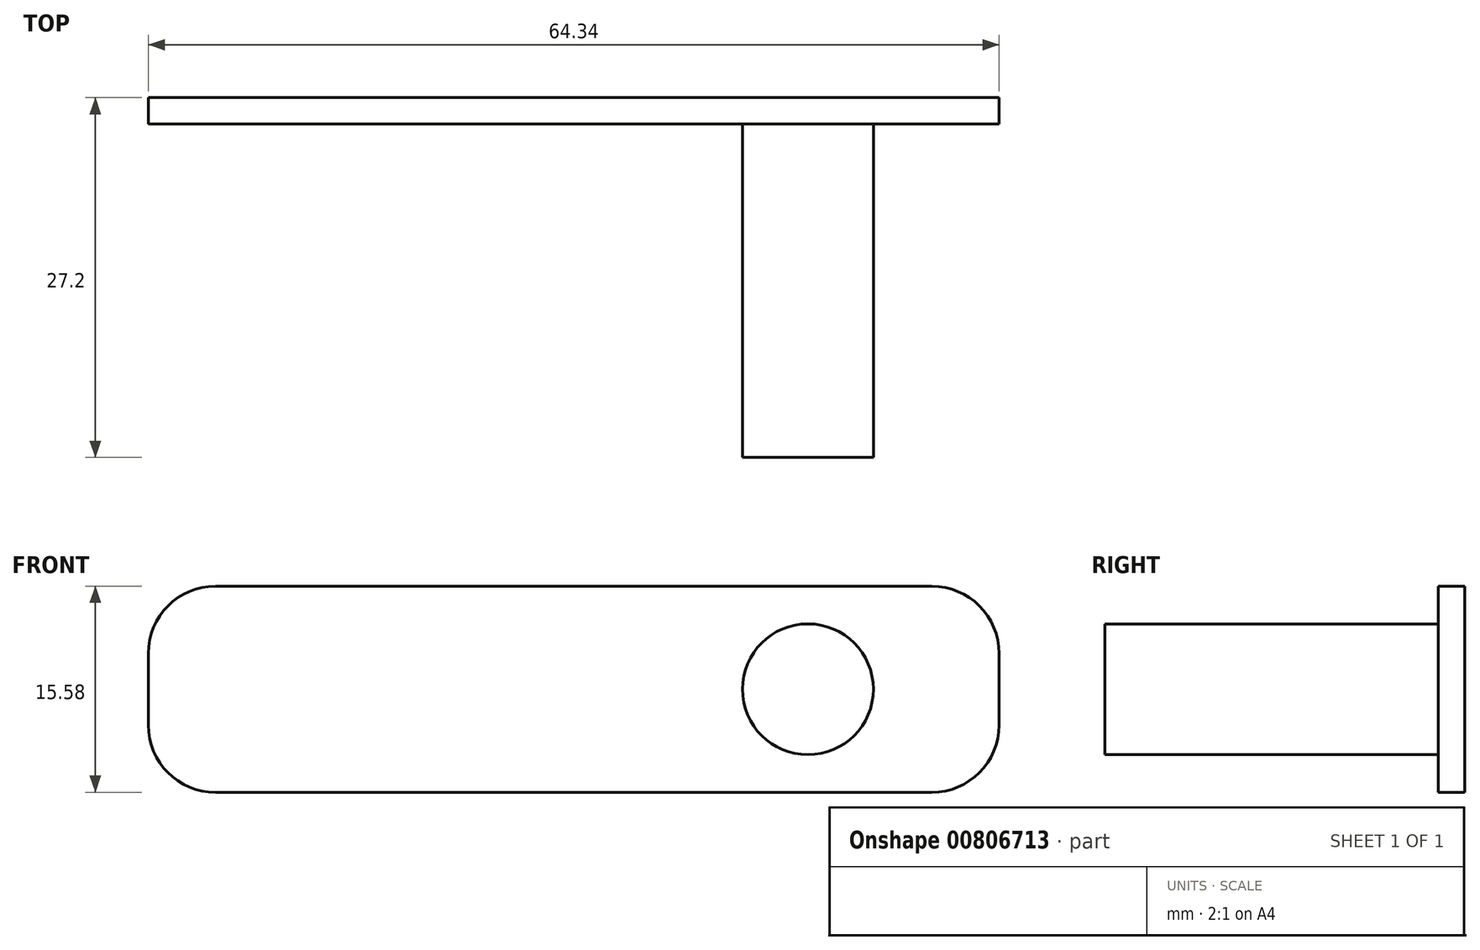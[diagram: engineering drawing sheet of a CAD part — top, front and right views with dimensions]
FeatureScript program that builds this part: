
annotation { "Feature Type Name" : "Feature", "Feature Type Description" : "" }
export const myFeature = defineFeature(function(context is Context, id is Id, definition is map)
    precondition{}
    {
        {
            var Q0;
            Q0=qCreatedBy(makeId("Front.planeOp"),FACE);
            var sketch = newSketch(context, id + "F0", { "sketchPlane" : qUnion([Q0])});
            skLineSegment(sketch, "E0.bottom", {"start": v(32.17, -7.8) * mm, "end": v(-32.17, -7.8) * mm});
            skLineSegment(sketch, "E0.top", {"start": v(32.17, 7.8) * mm, "end": v(-32.17, 7.8) * mm});
            skLineSegment(sketch, "E0.left", {"start": v(32.17, -7.8) * mm, "end": v(32.17, 7.8) * mm});
            skLineSegment(sketch, "E0.right", {"start": v(-32.17, -7.8) * mm, "end": v(-32.17, 7.8) * mm});
            skPoint(sketch, "E0.middle", {"position": v(0, 0) * mm});
            skSolve(sketch);
        }
        {
            var Q0;
            Q0=makeQuery(id+"F0.imprint","IMPRINT",FACE,{"disambiguationData":[TD([[makeQuery(id+"F0.imprint","IMPRINT",EDGE,{"derivedFrom":sQuery(id+"F0.wireOp",EDGE,"E0.bottom")}),-1.0]])]});
            extrude(context, id + "F1", {"entities" : qUnion([Q0]), "depth" : 2 * mm, "offsetDistance" : 25.4 * mm});
        }
        {
            var Q0;
            Q0=makeQuery(id+"F1.opExtrude","CAP_FACE",FACE,{"disambiguationData":[OSD([sQuery(id+"F0.wireOp",EDGE,"E0.bottom"),sQuery(id+"F0.wireOp",EDGE,"E0.top"),sQuery(id+"F0.wireOp",EDGE,"E0.left"),sQuery(id+"F0.wireOp",EDGE,"E0.right")])],"isStart":false});
            var sketch = newSketch(context, id + "F2", { "sketchPlane" : qUnion([Q0])});
            skCircle(sketch, "E1", {"center": v(17.71, 0) * mm, "radius": 4.95 * mm});
            skSolve(sketch);
        }
        {
            var Q0;
            Q0=makeQuery(id+"F2.imprint","IMPRINT",FACE,{"disambiguationData":[TD([[makeQuery(id+"F2.imprint","IMPRINT",EDGE,{"derivedFrom":sQuery(id+"F2.wireOp",EDGE,"E1")}),1.0]])]});
            extrude(context, id + "F3", {"entities" : qUnion([Q0]), "operationType" : NewBodyOperationType.ADD, "depth" : 25.2 * mm, "offsetDistance" : 25.4 * mm});
        }
        {
            var Q0;
            Q0=makeQuery(id+"F1.opExtrude","SWEPT_EDGE",EDGE,{"disambiguationData":[OSD([sQuery(id+"F0.wireOp",EDGE,"E0.bottom"),sQuery(id+"F0.wireOp",EDGE,"E0.right")])]});
            var Q1;
            Q1=makeQuery(id+"F1.opExtrude","SWEPT_EDGE",EDGE,{"disambiguationData":[OSD([sQuery(id+"F0.wireOp",EDGE,"E0.top"),sQuery(id+"F0.wireOp",EDGE,"E0.right")])]});
            var Q2;
            Q2=makeQuery(id+"F1.opExtrude","SWEPT_EDGE",EDGE,{"disambiguationData":[OSD([sQuery(id+"F0.wireOp",EDGE,"E0.bottom"),sQuery(id+"F0.wireOp",EDGE,"E0.left")])]});
            var Q3;
            Q3=makeQuery(id+"F1.opExtrude","SWEPT_EDGE",EDGE,{"disambiguationData":[OSD([sQuery(id+"F0.wireOp",EDGE,"E0.top"),sQuery(id+"F0.wireOp",EDGE,"E0.left")])]});
            fillet(context, id + "F4", {"entities" : qUnion([Q0, Q1, Q2, Q3]), "radius" : 5.08 * mm, "tangentPropagation" : true, "allowEdgeOverflow" : false});
        }
    });
